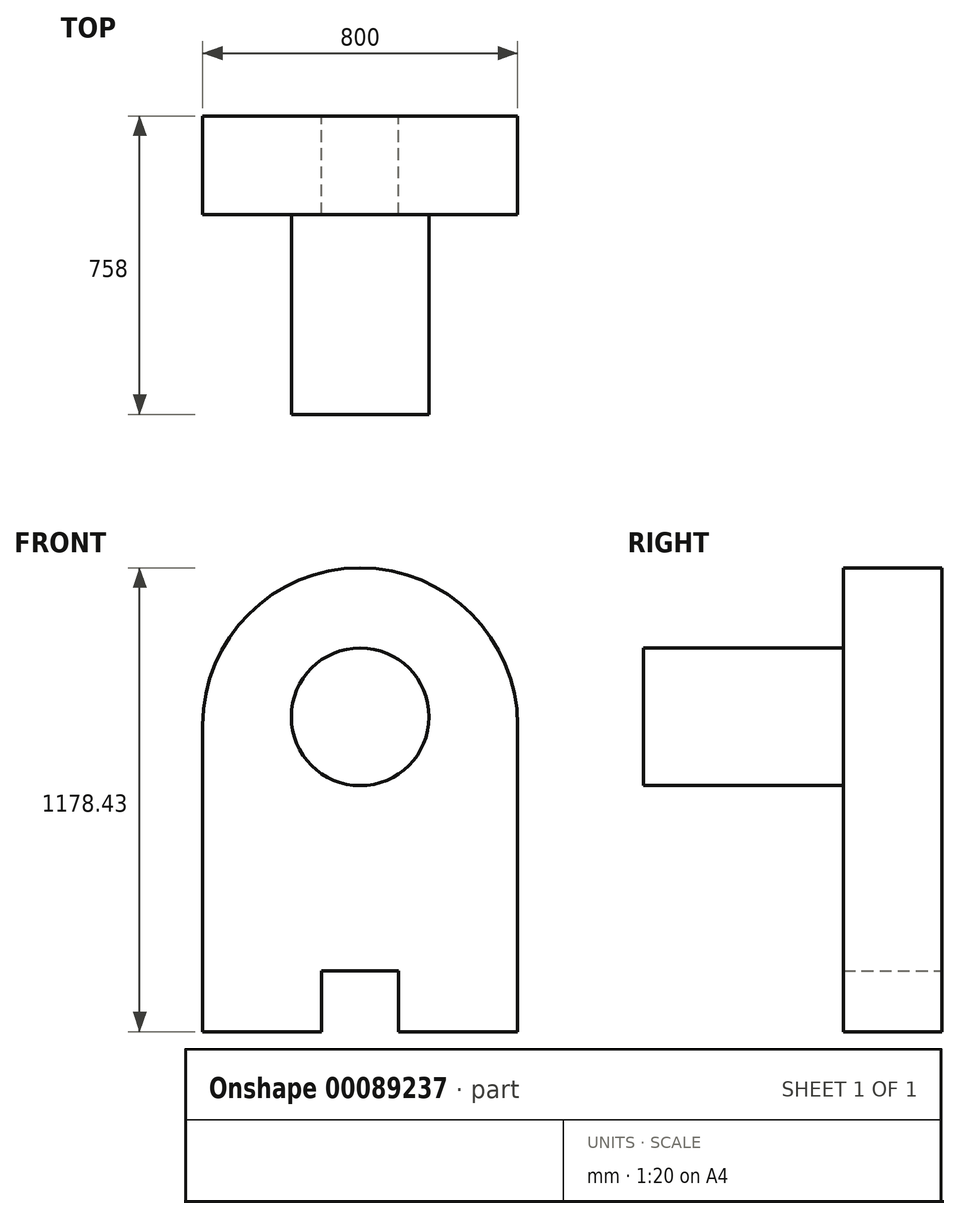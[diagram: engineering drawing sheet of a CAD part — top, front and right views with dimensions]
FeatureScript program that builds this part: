
annotation { "Feature Type Name" : "Feature", "Feature Type Description" : "" }
export const myFeature = defineFeature(function(context is Context, id is Id, definition is map)
    precondition{}
    {
        {
            var Q0;
            Q0=qCreatedBy(makeId("Front.planeOp"),FACE);
            var sketch = newSketch(context, id + "F0", { "sketchPlane" : qUnion([Q0])});
            skArc(sketch, "E0", {"start": v(400, -21.57) * mm, "mid": v(0, 378.43) * mm, "end": v(-400, -21.57) * mm});
            skLineSegment(sketch, "E1.bottom", {"start": v(400, -800) * mm, "end": v(-400, -800) * mm});
            skLineSegment(sketch, "E1.left", {"start": v(400, -800) * mm, "end": v(400, -21.57) * mm});
            skLineSegment(sketch, "E1.right", {"start": v(-400, -800) * mm, "end": v(-400, -21.57) * mm});
            skPoint(sketch, "E1.middle", {"position": v(0, 0) * mm});
            skPoint(sketch, "E1.top.end.orphan", {"position": v(-400, 800) * mm});
            skPoint(sketch, "E1.top.start.orphan", {"position": v(400, 800) * mm});
            skLineSegment(sketch, "E2.top", {"start": v(97.57, -645.61) * mm, "end": v(-97.57, -645.61) * mm});
            skLineSegment(sketch, "E2.left", {"start": v(97.57, -800) * mm, "end": v(97.57, -645.61) * mm});
            skLineSegment(sketch, "E2.right", {"start": v(-97.57, -800) * mm, "end": v(-97.57, -645.61) * mm});
            skPoint(sketch, "E2.middle", {"position": v(0, -800) * mm});
            skPoint(sketch, "E3.orphan", {"position": v(-97.57, -954.39) * mm});
            skPoint(sketch, "E4.orphan", {"position": v(97.57, -954.39) * mm});
            skSolve(sketch);
        }
        {
            var Q0;
            Q0=makeQuery(id+"F0.imprint","IMPRINT",FACE,{"disambiguationData":[TD([[makeQuery(id+"F0.imprint","IMPRINT",EDGE,{"derivedFrom":sQuery(id+"F0.wireOp",EDGE,"E0")}),1.0]])]});
            extrude(context, id + "F1", {"entities" : qUnion([Q0]), "endBound" : BoundingType.SYMMETRIC, "depth" : 250 * mm});
        }
        {
            var Q0;
            Q0=makeQuery(id+"F1.opExtrude","CAP_FACE",FACE,{"disambiguationData":[OSD([sQuery(id+"F0.wireOp",EDGE,"E0"),sQuery(id+"F0.wireOp",EDGE,"E1.bottom"),sQuery(id+"F0.wireOp",EDGE,"E1.left"),sQuery(id+"F0.wireOp",EDGE,"E1.right"),sQuery(id+"F0.wireOp",EDGE,"E2.top"),sQuery(id+"F0.wireOp",EDGE,"E2.left"),sQuery(id+"F0.wireOp",EDGE,"E2.right")])],"isStart":false});
            var sketch = newSketch(context, id + "F2", { "sketchPlane" : qUnion([Q0])});
            skCircle(sketch, "E5", {"center": v(0, 0) * mm, "radius": 175 * mm});
            skSolve(sketch);
        }
        {
            var Q0;
            Q0=makeQuery(id+"F2.imprint","IMPRINT",FACE,{"disambiguationData":[TD([[makeQuery(id+"F2.imprint","IMPRINT",EDGE,{"derivedFrom":sQuery(id+"F2.wireOp",EDGE,"E5")}),1.0]])]});
            extrude(context, id + "F3", {"entities" : qUnion([Q0]), "operationType" : NewBodyOperationType.ADD, "depth" : 508 * mm});
        }
    });
